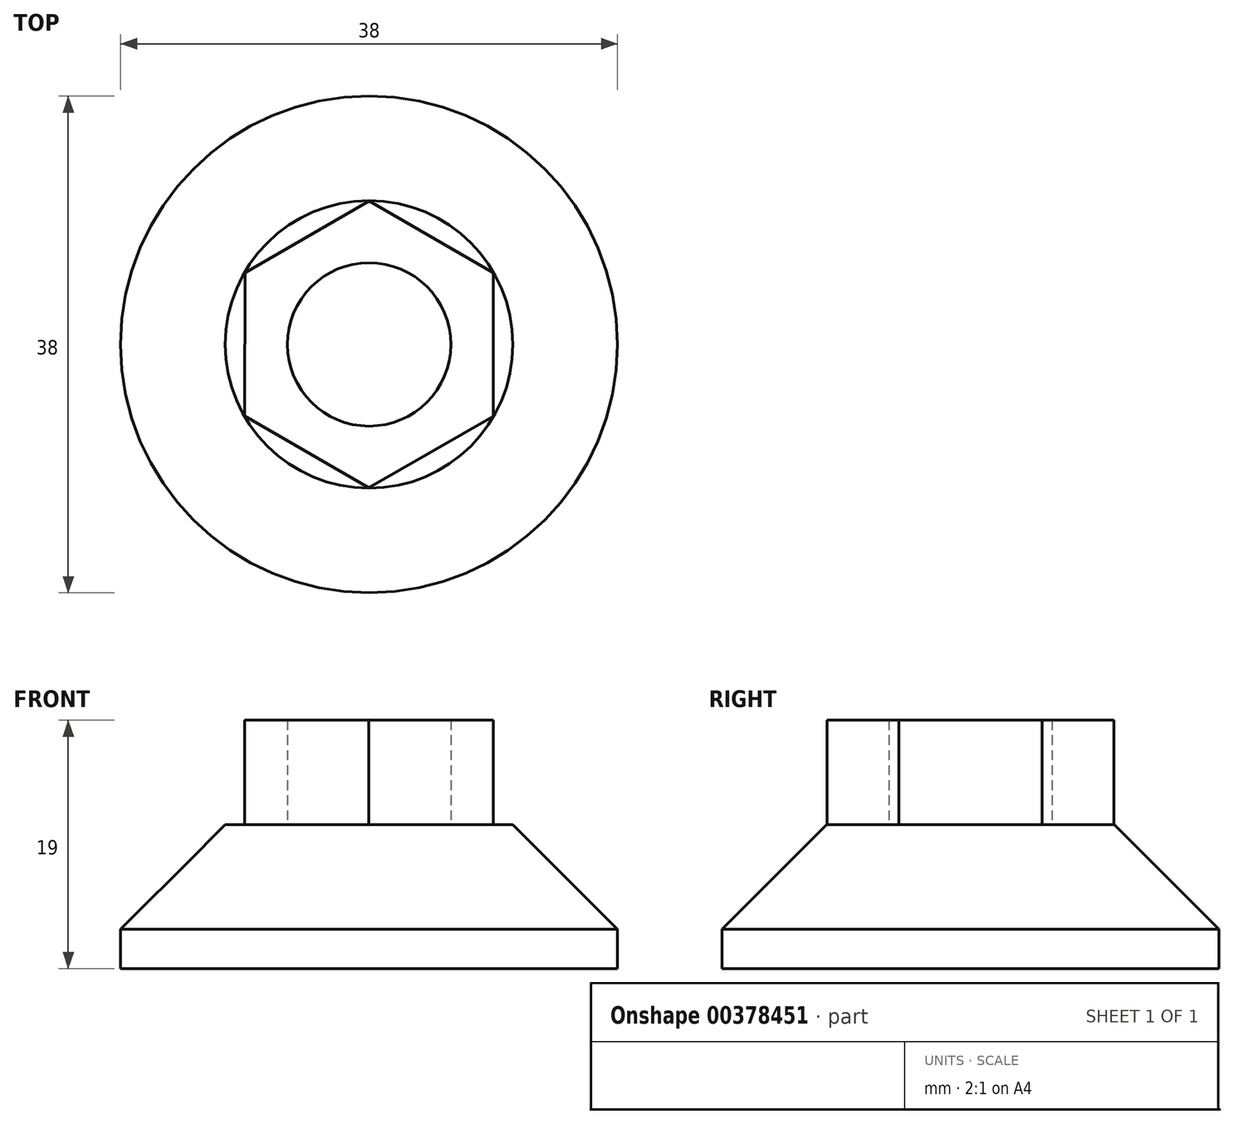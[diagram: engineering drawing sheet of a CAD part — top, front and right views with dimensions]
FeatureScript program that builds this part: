
annotation { "Feature Type Name" : "Feature", "Feature Type Description" : "" }
export const myFeature = defineFeature(function(context is Context, id is Id, definition is map)
    precondition{}
    {
        {
            var Q0;
            Q0=qCreatedBy(makeId("Top.planeOp"),FACE);
            var sketch = newSketch(context, id + "F0", { "sketchPlane" : qUnion([Q0])});
            skCircle(sketch, "E0.cCircle", {"center": v(0, 0) * mm, "radius": 10.97 * mm, "construction": true});
            skLineSegment(sketch, "E0.0", {"start": v(9.5, 5.48) * mm, "end": v(9.5, -5.5) * mm});
            skLineSegment(sketch, "E0.1", {"start": v(9.5, -5.5) * mm, "end": v(-0.01, -10.97) * mm});
            skLineSegment(sketch, "E0.2", {"start": v(-0.01, -10.97) * mm, "end": v(-9.5, -5.48) * mm});
            skLineSegment(sketch, "E0.3", {"start": v(-9.5, -5.48) * mm, "end": v(-9.5, 5.5) * mm});
            skLineSegment(sketch, "E0.4", {"start": v(-9.5, 5.5) * mm, "end": v(0.01, 10.97) * mm});
            skLineSegment(sketch, "E0.5", {"start": v(0.01, 10.97) * mm, "end": v(9.5, 5.48) * mm});
            skCircle(sketch, "E1", {"center": v(0, 0) * mm, "radius": 6.25 * mm});
            skSolve(sketch);
        }
        {
            var Q0;
            Q0 = qSketchRegion(id + "F0", true);
            extrude(context, id + "F1", {"entities" : qUnion([Q0]), "depth" : 8 * mm});
        }
        {
            var Q0;
            Q0=qCreatedBy(makeId("Right.planeOp"),FACE);
            var sketch = newSketch(context, id + "F2", { "sketchPlane" : qUnion([Q0])});
            skLineSegment(sketch, "E2", {"start": v(0, 0) * mm, "end": v(11, 0) * mm});
            skLineSegment(sketch, "E3", {"start": v(11, 0) * mm, "end": v(19, -8) * mm});
            skLineSegment(sketch, "E4", {"start": v(19, -8) * mm, "end": v(19, -11) * mm});
            skLineSegment(sketch, "E5", {"start": v(19, -11) * mm, "end": v(0, -11) * mm});
            skLineSegment(sketch, "E6", {"start": v(0, -11) * mm, "end": v(0, 0) * mm});
            skSolve(sketch);
        }
        {
            var Q0;
            Q0 = qSketchRegion(id + "F2", true);
            var Q1;
            Q1=sQuery(id+"F2.wireOp",EDGE,"E6");
            revolve(context, id + "F3", {"operationType" : NewBodyOperationType.ADD, "entities" : qUnion([Q0]), "axis" : qUnion([Q1]), "revolveType" : RevolveType.FULL});
        }
    });
